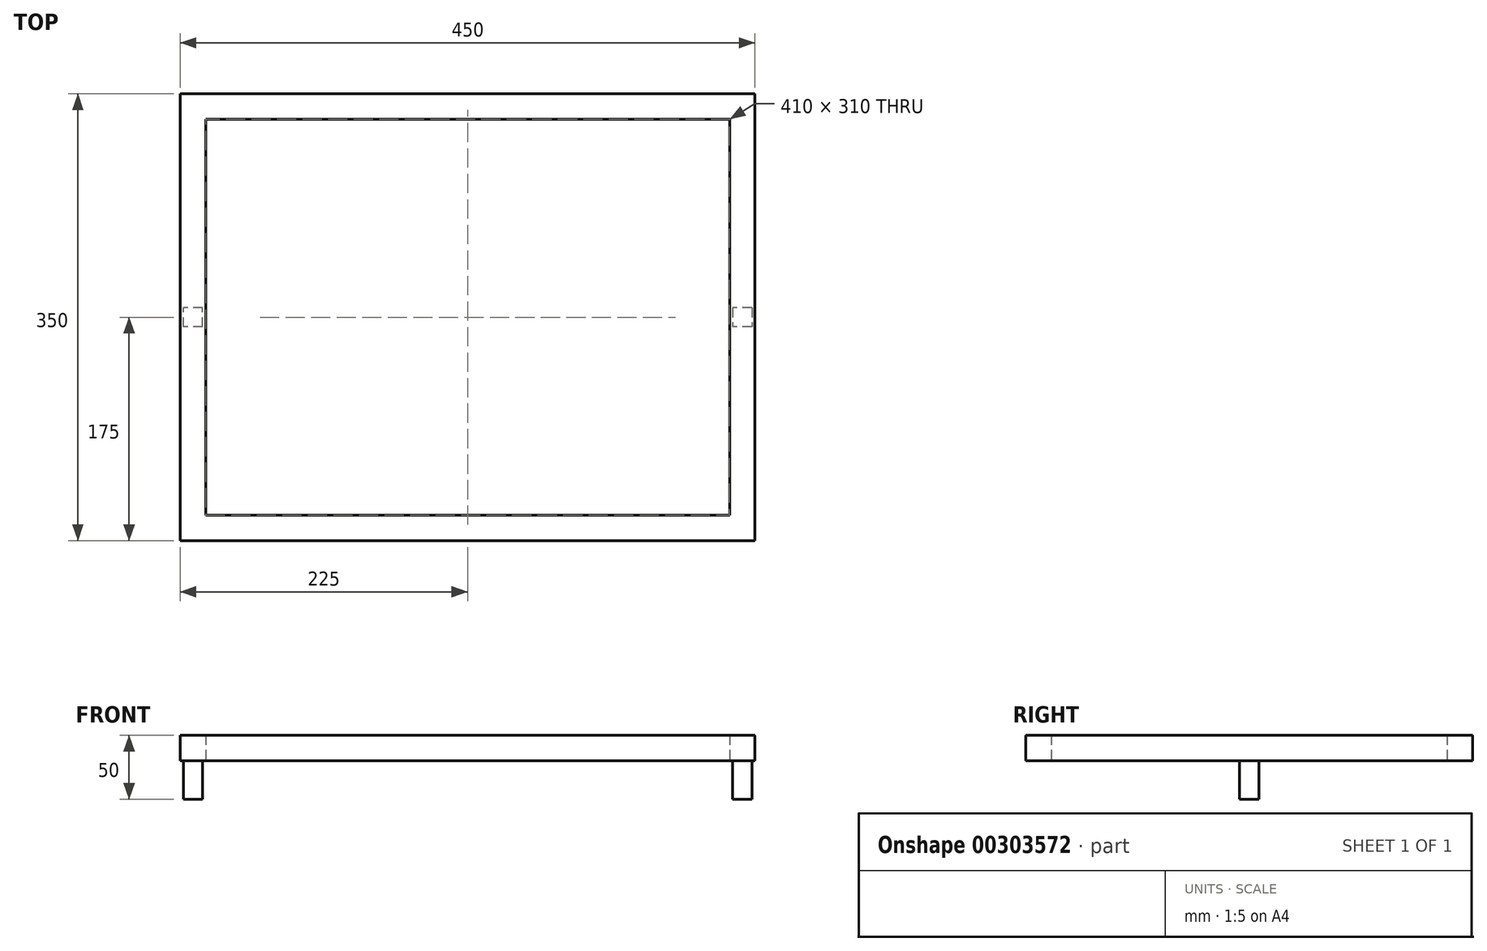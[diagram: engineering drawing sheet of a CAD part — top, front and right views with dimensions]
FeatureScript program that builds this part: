
annotation { "Feature Type Name" : "Feature", "Feature Type Description" : "" }
export const myFeature = defineFeature(function(context is Context, id is Id, definition is map)
    precondition{}
    {
        {
            var Q0;
            Q0=qCreatedBy(makeId("Top.planeOp"),FACE);
            var sketch = newSketch(context, id + "F0", { "sketchPlane" : qUnion([Q0])});
            skLineSegment(sketch, "E0.bottom", {"start": v(-225, 175) * mm, "end": v(225, 175) * mm});
            skLineSegment(sketch, "E0.top", {"start": v(-225, -175) * mm, "end": v(225, -175) * mm});
            skLineSegment(sketch, "E0.left", {"start": v(-225, 175) * mm, "end": v(-225, -175) * mm});
            skLineSegment(sketch, "E0.right", {"start": v(225, 175) * mm, "end": v(225, -175) * mm});
            skPoint(sketch, "E0.middle", {"position": v(0, 0) * mm});
            skLineSegment(sketch, "E1.0", {"start": v(-205, 155) * mm, "end": v(205, 155) * mm});
            skLineSegment(sketch, "E1.1", {"start": v(-205, 155) * mm, "end": v(-205, -155) * mm});
            skLineSegment(sketch, "E1.2", {"start": v(-205, -155) * mm, "end": v(205, -155) * mm});
            skLineSegment(sketch, "E1.3", {"start": v(205, 155) * mm, "end": v(205, -155) * mm});
            skSolve(sketch);
        }
        {
            var Q0;
            Q0=makeQuery(id+"F0.imprint","IMPRINT",FACE,{"disambiguationData":[TD([[makeQuery(id+"F0.imprint","IMPRINT",EDGE,{"derivedFrom":sQuery(id+"F0.wireOp",EDGE,"E0.bottom")}),-1.0]])]});
            extrude(context, id + "F1", {"entities" : qUnion([Q0]), "depth" : 20 * mm});
        }
        {
            var Q0;
            Q0=makeQuery(id+"F1.opExtrude","CAP_FACE",FACE,{"disambiguationData":[OSD([sQuery(id+"F0.wireOp",EDGE,"E0.bottom"),sQuery(id+"F0.wireOp",EDGE,"E0.top"),sQuery(id+"F0.wireOp",EDGE,"E0.left"),sQuery(id+"F0.wireOp",EDGE,"E0.right"),sQuery(id+"F0.wireOp",EDGE,"E1.0"),sQuery(id+"F0.wireOp",EDGE,"E1.1"),sQuery(id+"F0.wireOp",EDGE,"E1.2"),sQuery(id+"F0.wireOp",EDGE,"E1.3")])],"isStart":true});
            var sketch = newSketch(context, id + "F2", { "sketchPlane" : qUnion([Q0])});
            skLineSegment(sketch, "E2", {"start": v(-225, 175) * mm, "end": v(-264.47, 175) * mm, "construction": true});
            skLineSegment(sketch, "E3", {"start": v(-264.47, 175) * mm, "end": v(-264.47, -175) * mm, "construction": true});
            skLineSegment(sketch, "E4", {"start": v(-264.47, 0) * mm, "end": v(-225, 0) * mm, "construction": true});
            skLineSegment(sketch, "E5", {"start": v(-205, 0) * mm, "end": v(-225, 0) * mm, "construction": true});
            skPoint(sketch, "E6.middle", {"position": v(-215, 0) * mm});
            skLineSegment(sketch, "E7.bottom", {"start": v(-207.5, 7.5) * mm, "end": v(-222.5, 7.5) * mm});
            skLineSegment(sketch, "E7.top", {"start": v(-207.5, -7.5) * mm, "end": v(-222.5, -7.5) * mm});
            skLineSegment(sketch, "E7.left", {"start": v(-207.5, 7.5) * mm, "end": v(-207.5, -7.5) * mm});
            skLineSegment(sketch, "E7.right", {"start": v(-222.5, 7.5) * mm, "end": v(-222.5, -7.5) * mm});
            skLineSegment(sketch, "E8", {"start": v(-205, 0) * mm, "end": v(205, 0) * mm, "construction": true});
            skLineSegment(sketch, "E9", {"start": v(205, 0) * mm, "end": v(225, 0) * mm, "construction": true});
            skLineSegment(sketch, "E10.bottom", {"start": v(222.5, -7.5) * mm, "end": v(207.5, -7.5) * mm});
            skLineSegment(sketch, "E10.top", {"start": v(222.5, 7.5) * mm, "end": v(207.5, 7.5) * mm});
            skLineSegment(sketch, "E10.left", {"start": v(222.5, -7.5) * mm, "end": v(222.5, 7.5) * mm});
            skLineSegment(sketch, "E10.right", {"start": v(207.5, -7.5) * mm, "end": v(207.5, 7.5) * mm});
            skPoint(sketch, "E10.middle", {"position": v(215, 0) * mm});
            skSolve(sketch);
        }
        {
            var Q0;
            Q0=makeQuery(id+"F2.imprint","IMPRINT",FACE,{"disambiguationData":[TD([[makeQuery(id+"F2.imprint","IMPRINT",EDGE,{"derivedFrom":sQuery(id+"F2.wireOp",EDGE,"E7.bottom")}),1.0]])]});
            var Q1;
            Q1=makeQuery(id+"F2.imprint","IMPRINT",FACE,{"disambiguationData":[TD([[makeQuery(id+"F2.imprint","IMPRINT",EDGE,{"derivedFrom":sQuery(id+"F2.wireOp",EDGE,"E10.bottom")}),-1.0]])]});
            extrude(context, id + "F3", {"entities" : qUnion([Q0, Q1]), "operationType" : NewBodyOperationType.ADD, "depth" : 30 * mm});
        }
    });
